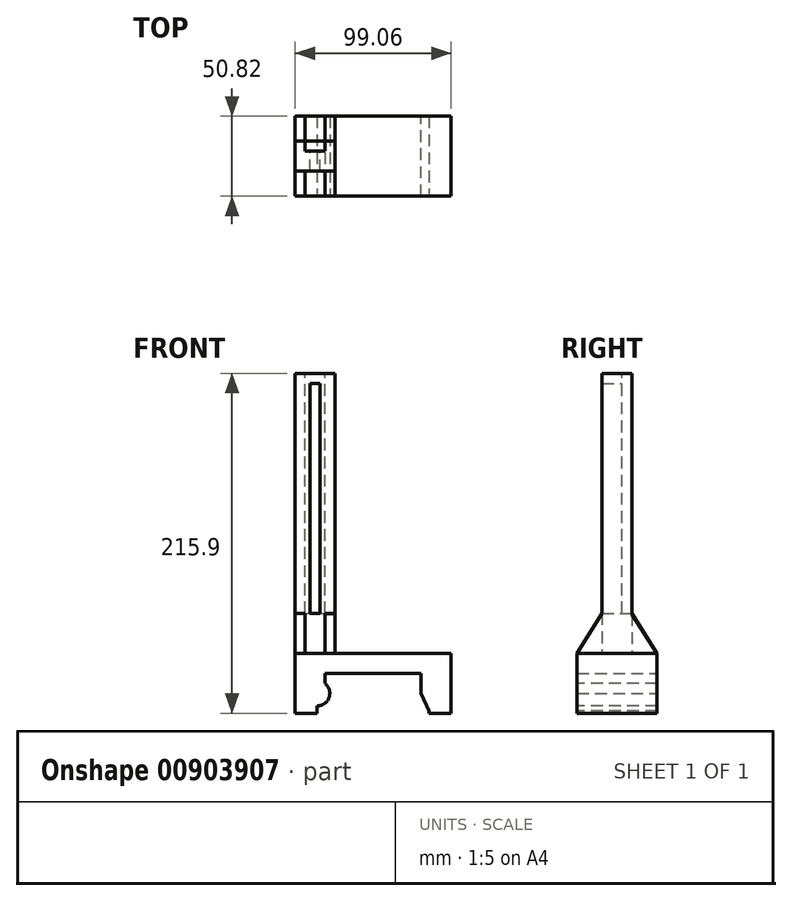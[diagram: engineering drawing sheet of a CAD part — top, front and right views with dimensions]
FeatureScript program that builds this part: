
annotation { "Feature Type Name" : "Feature", "Feature Type Description" : "" }
export const myFeature = defineFeature(function(context is Context, id is Id, definition is map)
    precondition{}
    {
        {
            var Q0;
            Q0=qCreatedBy(makeId("Front.planeOp"),FACE);
            var sketch = newSketch(context, id + "F0", { "sketchPlane" : qUnion([Q0])});
            skLineSegment(sketch, "E0.bottom", {"start": v(49.53, -19.05) * mm, "end": v(-49.53, -19.05) * mm});
            skLineSegment(sketch, "E0.top", {"start": v(49.53, 19.05) * mm, "end": v(-49.53, 19.05) * mm});
            skLineSegment(sketch, "E0.left", {"start": v(49.53, -19.05) * mm, "end": v(49.53, 19.05) * mm});
            skLineSegment(sketch, "E0.right", {"start": v(-49.53, -19.05) * mm, "end": v(-49.53, 19.05) * mm});
            skPoint(sketch, "E0.middle", {"position": v(0, 0) * mm});
            skLineSegment(sketch, "E1.bottom", {"start": v(30.48, -44.45) * mm, "end": v(-30.48, -44.45) * mm});
            skLineSegment(sketch, "E1.top", {"start": v(30.48, 6.35) * mm, "end": v(-30.48, 6.35) * mm});
            skLineSegment(sketch, "E1.left", {"start": v(30.48, -44.45) * mm, "end": v(30.48, 6.35) * mm});
            skLineSegment(sketch, "E1.right", {"start": v(-30.48, -44.45) * mm, "end": v(-30.48, 6.35) * mm});
            skPoint(sketch, "E1.middle", {"position": v(0, -19.05) * mm});
            skSolve(sketch);
        }
        {
            var Q0;
            Q0=makeQuery(id+"F0.imprint","IMPRINT",FACE,{"disambiguationData":[TD([[makeQuery(id+"F0.imprint","IMPRINT",EDGE,{"derivedFrom":sQuery(id+"F0.wireOp",EDGE,"E0.top")}),1.0]])]});
            extrude(context, id + "F1", {"entities" : qUnion([Q0]), "endBound" : BoundingType.SYMMETRIC, "depth" : 50.8 * mm, "offsetDistance" : 25.4 * mm});
        }
        {
            var Q0;
            Q0=qCreatedBy(makeId("Front.planeOp"),FACE);
            var sketch = newSketch(context, id + "F2", { "sketchPlane" : qUnion([Q0])});
            skLineSegment(sketch, "E2.bottom", {"start": v(35.56, -33.74) * mm, "end": v(-35.56, -33.74) * mm});
            skLineSegment(sketch, "E2.top", {"start": v(35.56, -6.35) * mm, "end": v(-35.56, -6.35) * mm});
            skLineSegment(sketch, "E2.left", {"start": v(35.56, -33.74) * mm, "end": v(35.56, -6.35) * mm});
            skLineSegment(sketch, "E2.right", {"start": v(-35.56, -33.74) * mm, "end": v(-35.56, -6.35) * mm});
            skPoint(sketch, "E2.middle", {"position": v(0, -20.05) * mm});
            skSolve(sketch);
        }
        {
            var Q0;
            Q0=makeQuery(id+"F2.imprint","IMPRINT",FACE,{"disambiguationData":[TD([[makeQuery(id+"F2.imprint","IMPRINT",EDGE,{"derivedFrom":sQuery(id+"F2.wireOp",EDGE,"E2.bottom")}),-1.0]])]});
            extrude(context, id + "F3", {"entities" : qUnion([Q0]), "operationType" : NewBodyOperationType.REMOVE, "endBound" : BoundingType.SYMMETRIC, "oppositeDirection" : true, "depth" : 101.6 * mm, "offsetDistance" : 25.4 * mm});
        }
        {
            var Q0;
            Q0=makeQuery(id+"FqtUo2dF14dtISF_1.boolean.opBoolean","MERGE",FACE,{"derivedFrom":[makeQuery(id+"F1.opExtrude","CAP_FACE",FACE,{"disambiguationData":[OSD([sQuery(id+"F0.wireOp",EDGE,"E0.bottom"),sQuery(id+"F0.wireOp",EDGE,"E0.top"),sQuery(id+"F0.wireOp",EDGE,"E0.left"),sQuery(id+"F0.wireOp",EDGE,"E0.right"),sQuery(id+"F0.wireOp",EDGE,"E1.top"),sQuery(id+"F0.wireOp",EDGE,"E1.left"),sQuery(id+"F0.wireOp",EDGE,"E1.right")])],"isStart":false}),makeQuery(id+"FqtUo2dF14dtISF_1.opExtrude","CAP_FACE",FACE,{"disambiguationData":[OSD([sQuery(id+"Fa6pJ2o9r3T1tcu_1.wireOp",EDGE,"9ab49e5e-e781-4880-a481-f387394318e1.bottom"),sQuery(id+"Fa6pJ2o9r3T1tcu_1.wireOp",EDGE,"9ab49e5e-e781-4880-a481-f387394318e1.top"),sQuery(id+"Fa6pJ2o9r3T1tcu_1.wireOp",EDGE,"9ab49e5e-e781-4880-a481-f387394318e1.left"),sQuery(id+"Fa6pJ2o9r3T1tcu_1.wireOp",EDGE,"HMghRU8G-1H3M-OJ5W-wMgI-K1z1DDckNYTP"),sQuery(id+"Fa6pJ2o9r3T1tcu_1.wireOp",EDGE,"0KJWoq3j-ts2y-bZzM-44IR-2JegtjsgD1qJ")])],"isStart":true})]});
            var sketch = newSketch(context, id + "F4", { "sketchPlane" : qUnion([Q0])});
            skCircle(sketch, "E3", {"center": v(-35.56, -6.35) * mm, "radius": 8.06 * mm});
            skSolve(sketch);
        }
        {
            var Q0;
            Q0=qSketchRegion(id+"F4",true);
            extrude(context, id + "F5", {"entities" : qUnion([Q0]), "operationType" : NewBodyOperationType.ADD, "oppositeDirection" : true, "depth" : 50.8 * mm, "offsetDistance" : 25.4 * mm});
        }
        {
            var Q0;
            Q0=makeQuery(id+"F5.boolean.opBoolean","MERGE",FACE,{"derivedFrom":[makeQuery(id+"FqtUo2dF14dtISF_1.boolean.opBoolean","MERGE",FACE,{"derivedFrom":[makeQuery(id+"F1.opExtrude","CAP_FACE",FACE,{"disambiguationData":[OSD([sQuery(id+"F0.wireOp",EDGE,"E0.bottom"),sQuery(id+"F0.wireOp",EDGE,"E0.top"),sQuery(id+"F0.wireOp",EDGE,"E0.left"),sQuery(id+"F0.wireOp",EDGE,"E0.right"),sQuery(id+"F0.wireOp",EDGE,"E1.top"),sQuery(id+"F0.wireOp",EDGE,"E1.left"),sQuery(id+"F0.wireOp",EDGE,"E1.right")])],"isStart":false}),makeQuery(id+"FqtUo2dF14dtISF_1.opExtrude","CAP_FACE",FACE,{"disambiguationData":[OSD([sQuery(id+"Fa6pJ2o9r3T1tcu_1.wireOp",EDGE,"9ab49e5e-e781-4880-a481-f387394318e1.bottom"),sQuery(id+"Fa6pJ2o9r3T1tcu_1.wireOp",EDGE,"9ab49e5e-e781-4880-a481-f387394318e1.top"),sQuery(id+"Fa6pJ2o9r3T1tcu_1.wireOp",EDGE,"9ab49e5e-e781-4880-a481-f387394318e1.left"),sQuery(id+"Fa6pJ2o9r3T1tcu_1.wireOp",EDGE,"HMghRU8G-1H3M-OJ5W-wMgI-K1z1DDckNYTP"),sQuery(id+"Fa6pJ2o9r3T1tcu_1.wireOp",EDGE,"0KJWoq3j-ts2y-bZzM-44IR-2JegtjsgD1qJ")])],"isStart":true})]}),makeQuery(id+"F5.opExtrude","CAP_FACE",FACE,{"disambiguationData":[OSD([sQuery(id+"F4.wireOp",EDGE,"E3")])],"isStart":true})]});
            var sketch = newSketch(context, id + "F6", { "sketchPlane" : qUnion([Q0])});
            skLineSegment(sketch, "E4", {"start": v(35.56, -6.35) * mm, "end": v(35.56, -17.47) * mm});
            skLineSegment(sketch, "E5", {"start": v(35.56, -17.47) * mm, "end": v(30.48, -6.35) * mm});
            skLineSegment(sketch, "E6", {"start": v(30.48, -6.35) * mm, "end": v(35.56, -6.35) * mm});
            skSolve(sketch);
        }
        {
            var Q0;
            Q0=qSketchRegion(id+"F6",true);
            extrude(context, id + "F7", {"entities" : qUnion([Q0]), "operationType" : NewBodyOperationType.ADD, "oppositeDirection" : true, "depth" : 50.8 * mm, "offsetDistance" : 25.4 * mm});
        }
        {
            var Q0;
            Q0=makeQuery(id+"F1.opExtrude","SWEPT_FACE",FACE,{"disambiguationData":[OSD([sQuery(id+"F0.wireOp",EDGE,"E0.top")])]});
            var sketch = newSketch(context, id + "F8", { "sketchPlane" : qUnion([Q0])});
            skLineSegment(sketch, "E7.bottom", {"start": v(-24.13, 9.53) * mm, "end": v(-49.53, 9.53) * mm});
            skLineSegment(sketch, "E7.top", {"start": v(-24.13, -9.52) * mm, "end": v(-49.53, -9.52) * mm});
            skLineSegment(sketch, "E7.left", {"start": v(-24.13, 9.53) * mm, "end": v(-24.13, -9.52) * mm});
            skLineSegment(sketch, "E7.right", {"start": v(-49.53, 9.53) * mm, "end": v(-49.53, -9.52) * mm});
            skPoint(sketch, "E7.middle", {"position": v(-36.83, 0) * mm});
            skSolve(sketch);
        }
        {
            var Q0;
            Q0 = qSketchRegion(id + "F8", true);
            extrude(context, id + "F9", {"entities" : qUnion([Q0]), "operationType" : NewBodyOperationType.ADD, "depth" : 177.8 * mm, "offsetDistance" : 25.4 * mm});
        }
        {
            var Q0;
            Q0=makeQuery(id+"F9.opExtrude","SWEPT_FACE",FACE,{"disambiguationData":[OSD([sQuery(id+"F8.wireOp",EDGE,"E7.bottom")])]});
            var sketch = newSketch(context, id + "F10", { "sketchPlane" : qUnion([Q0])});
            skLineSegment(sketch, "E8.bottom", {"start": v(43.18, 44.45) * mm, "end": v(30.48, 44.45) * mm});
            skLineSegment(sketch, "E8.top", {"start": v(43.18, 222.25) * mm, "end": v(30.48, 222.25) * mm});
            skLineSegment(sketch, "E8.left", {"start": v(43.18, 44.45) * mm, "end": v(43.18, 222.25) * mm});
            skLineSegment(sketch, "E8.right", {"start": v(30.48, 44.45) * mm, "end": v(30.48, 222.25) * mm});
            skPoint(sketch, "E8.middle", {"position": v(36.83, 133.35) * mm});
            skSolve(sketch);
        }
        {
            var Q0;
            Q0 = qSketchRegion(id + "F10", true);
            extrude(context, id + "F11", {"entities" : qUnion([Q0]), "operationType" : NewBodyOperationType.REMOVE, "oppositeDirection" : true, "depth" : 6.35 * mm, "offsetDistance" : 25.4 * mm});
        }
        {
            var Q0;
            Q0=makeQuery(id+"F11.boolean.opBoolean","COPY",FACE,{"derivedFrom":makeQuery(id+"F11.opExtrude","CAP_FACE",FACE,{"disambiguationData":[OSD([sQuery(id+"F10.wireOp",EDGE,"E8.bottom"),sQuery(id+"F10.wireOp",EDGE,"E8.top"),sQuery(id+"F10.wireOp",EDGE,"E8.left"),sQuery(id+"F10.wireOp",EDGE,"E8.right")])],"isStart":false})});
            var sketch = newSketch(context, id + "F12", { "sketchPlane" : qUnion([Q0])});
            skLineSegment(sketch, "E9.bottom", {"start": v(40, 44.45) * mm, "end": v(33.66, 44.45) * mm});
            skLineSegment(sketch, "E9.top", {"start": v(40, 190.5) * mm, "end": v(33.66, 190.5) * mm});
            skLineSegment(sketch, "E9.left", {"start": v(40, 44.45) * mm, "end": v(40, 190.5) * mm});
            skLineSegment(sketch, "E9.right", {"start": v(33.66, 44.45) * mm, "end": v(33.66, 190.5) * mm});
            skPoint(sketch, "E9.middle", {"position": v(36.83, 117.48) * mm});
            skSolve(sketch);
        }
        {
            var Q0;
            Q0 = qSketchRegion(id + "F12", true);
            extrude(context, id + "F13", {"entities" : qUnion([Q0]), "operationType" : NewBodyOperationType.REMOVE, "endBound" : BoundingType.THROUGH_ALL, "oppositeDirection" : true, "depth" : 25.4 * mm, "offsetDistance" : 25.4 * mm});
        }
        {
            var Q0;
            Q0=makeQuery(id+"F9.boolean.opBoolean","MERGE",FACE,{"derivedFrom":[makeQuery(id+"F1.opExtrude","SWEPT_FACE",FACE,{"disambiguationData":[OSD([sQuery(id+"F0.wireOp",EDGE,"E0.right")])]}),makeQuery(id+"F9.opExtrude","SWEPT_FACE",FACE,{"disambiguationData":[OSD([sQuery(id+"F8.wireOp",EDGE,"E7.right")])]})]});
            var sketch = newSketch(context, id + "F14", { "sketchPlane" : qUnion([Q0])});
            skLineSegment(sketch, "E10", {"start": v(-9.52, 19.05) * mm, "end": v(-9.52, 44.45) * mm});
            skLineSegment(sketch, "E11", {"start": v(-9.52, 19.05) * mm, "end": v(-25.4, 19.05) * mm});
            skLineSegment(sketch, "E12", {"start": v(-25.4, 19.05) * mm, "end": v(-9.52, 44.45) * mm});
            skLineSegment(sketch, "E13", {"start": v(9.53, 19.05) * mm, "end": v(9.53, 44.45) * mm});
            skLineSegment(sketch, "E14", {"start": v(25.4, 19.05) * mm, "end": v(9.52, 44.45) * mm});
            skSolve(sketch);
        }
        {
            var Q0;
            Q0=makeQuery(id+"F14.imprint","IMPRINT",FACE,{"disambiguationData":[TD([[makeQuery(id+"F14.imprint","IMPRINT",EDGE,{"derivedFrom":sQuery(id+"F14.wireOp",EDGE,"E10")}),-1.0]])]});
            var Q1;
            Q1=makeQuery(id+"F14.imprint","IMPRINT",FACE,{"disambiguationData":[TD([[makeQuery(id+"F14.imprint","IMPRINT",EDGE,{"derivedFrom":sQuery(id+"F14.wireOp",EDGE,"E13")}),1.0]])]});
            extrude(context, id + "F15", {"entities" : qUnion([Q0, Q1]), "operationType" : NewBodyOperationType.ADD, "oppositeDirection" : true, "depth" : 6.35 * mm, "offsetDistance" : 25.4 * mm});
        }
        {
            var Q0;
            Q0=makeQuery(id+"F9.opExtrude","SWEPT_FACE",FACE,{"disambiguationData":[OSD([sQuery(id+"F8.wireOp",EDGE,"E7.left")])]});
            var sketch = newSketch(context, id + "F16", { "sketchPlane" : qUnion([Q0])});
            skLineSegment(sketch, "E15", {"start": v(-9.52, 19.05) * mm, "end": v(-25.34, 19.05) * mm});
            skLineSegment(sketch, "E16", {"start": v(-9.52, 19.05) * mm, "end": v(-9.52, 44.45) * mm});
            skLineSegment(sketch, "E17", {"start": v(-9.52, 44.45) * mm, "end": v(-25.34, 19.05) * mm});
            skLineSegment(sketch, "E18", {"start": v(9.53, 19.05) * mm, "end": v(9.53, 43.85) * mm});
            skLineSegment(sketch, "E19", {"start": v(9.53, 19.05) * mm, "end": v(25.42, 19.05) * mm});
            skLineSegment(sketch, "E20", {"start": v(25.42, 19.05) * mm, "end": v(9.53, 43.85) * mm});
            skSolve(sketch);
        }
        {
            var Q0;
            Q0 = qSketchRegion(id + "F16", true);
            extrude(context, id + "F17", {"entities" : qUnion([Q0]), "operationType" : NewBodyOperationType.ADD, "oppositeDirection" : true, "depth" : 6.35 * mm, "offsetDistance" : 25.4 * mm});
        }
    });
